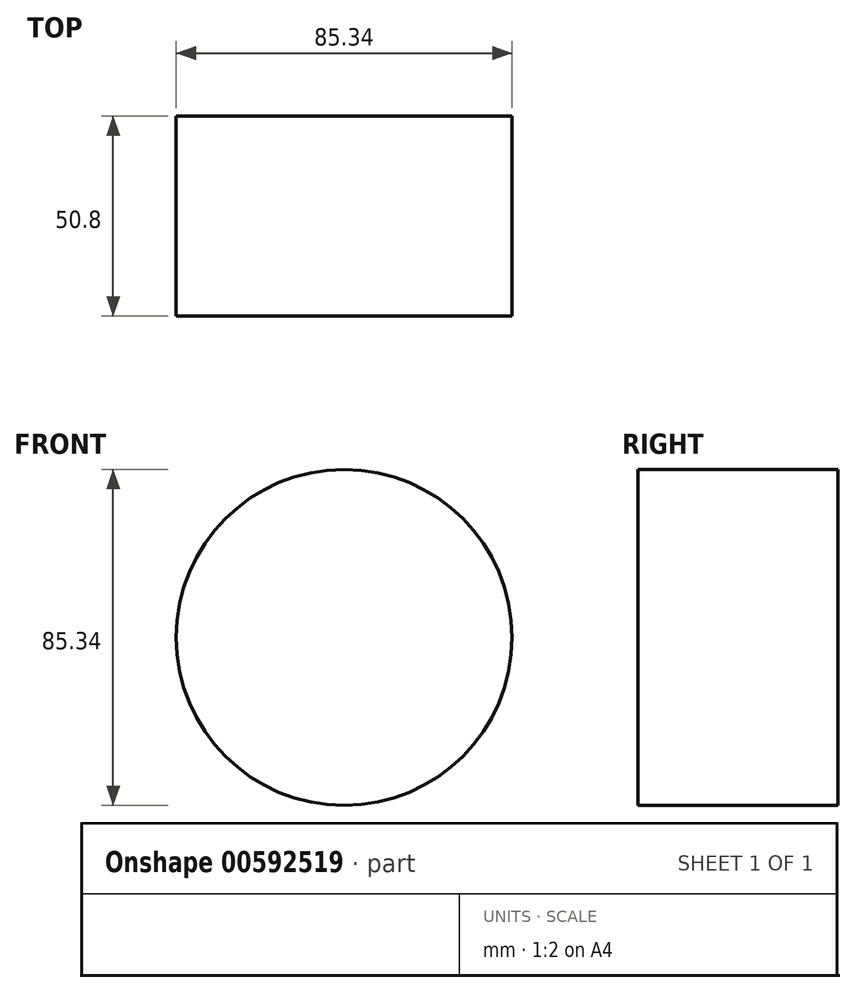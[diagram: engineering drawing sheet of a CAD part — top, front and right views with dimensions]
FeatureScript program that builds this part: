
annotation { "Feature Type Name" : "Feature", "Feature Type Description" : "" }
export const myFeature = defineFeature(function(context is Context, id is Id, definition is map)
    precondition{}
    {
        {
            var Q0;
            Q0=qCreatedBy(makeId("Front.planeOp"),FACE);
            var sketch = newSketch(context, id + "F0", { "sketchPlane" : qUnion([Q0])});
            skCircle(sketch, "E0", {"center": v(0, 0) * mm, "radius": 42.67 * mm});
            skCircle(sketch, "E1", {"center": v(55.63, 59.2) * mm, "radius": 10.7 * mm});
            skSolve(sketch);
        }
        {
            var Q0;
            Q0=makeQuery(id+"F0.imprint","IMPRINT",FACE,{"disambiguationData":[TD([[makeQuery(id+"F0.imprint","IMPRINT",EDGE,{"derivedFrom":sQuery(id+"F0.wireOp",EDGE,"E0")}),1.0]])]});
            extrude(context, id + "F1", {"entities" : qUnion([Q0]), "depth" : 50.8 * mm, "offsetDistance" : 25.4 * mm});
        }
    });
